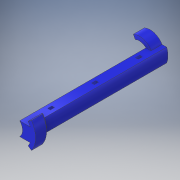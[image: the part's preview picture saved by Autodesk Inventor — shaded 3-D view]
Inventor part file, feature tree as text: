
AUTODESK INVENTOR PART (.ipt)
format: ipt  version: 2017 (Build 210142000, 142)  size: 206,336 bytes
history: native  units: in
note: dims shown in document units (in); Inventor stores cm internally (conversion verified against a paired STEP export)
features: sketch x7, extrude x5, revolve x2, chamfer x2, pattern_linear x1, plane x1
ambient origin geometry x8: Origin, YZ Plane, XZ Plane, XY Plane, X Axis, Y Axis, Z Axis, Center Point
bodies: Solid1 (feature_tree)
feature tree (18):
  extrude  "Extrusion1"  Depth=1.063in
  extrude  "Extrusion2"  Depth=0.2405in
  extrude  "Extrusion4"  Depth=0.3937in
  extrude  "Extrusion5"  Depth=3.937in TaperAngle=0.0deg
  revolve  "Revolution4"  [1 undecoded]
  pattern_linear  "Rectangular Pattern2"  Count1=10 Spacing1=0.0in
  plane  "Work Plane1"
  revolve  "Revolution5"  [1 undecoded]
  extrude  "Extrusion8"  Depth=0.5906in
  chamfer  "Chamfer2"  Distance=0.0787in
  chamfer  "Chamfer3"  Angle=90.0deg  [1 undecoded]
  sketch  "Sketch1"  dims[d0=1.2992in d1=1.063in]
  sketch  "Sketch2"  dims[d2=0.2405in d3=0.2405in]
  sketch  "Sketch4"  dims[d4=0.3937in d5=0.0in d6=0.3937in]
  sketch  "Sketch5"  dims[d7=0.3937in d8=3.937in d9=0.0in]
  sketch  "Sketch9"  dims[d14=1.0236in d15=3.937in d16=0.0in]
  sketch  "Sketch10"  dims[d17=0.5512in d18=3.937in d19=0.0in]
  sketch  "Sketch12"  dims[d34=0.063in d35=0.1181in d36=0.5906in d37=0.0787in d38=90.0deg d39=1.1811in d41=1.2598in d42=0.0in d43=0.1181in d44=0.315in d45=90.0deg d53=0.4466in d54=0.4466in d56=0.5118in d57=0.4724in d58=0.3937in d59=0.0in d63=0.0787in d64=0.0787in d65=45.0deg d66=0.0394in d67=0.0787in d68=45.0deg]
note: 3 required parameter values undecoded (feature->parameter linkage not recoverable at this tier; creation-order binding heuristic only, values carry confidence <= 0.55)